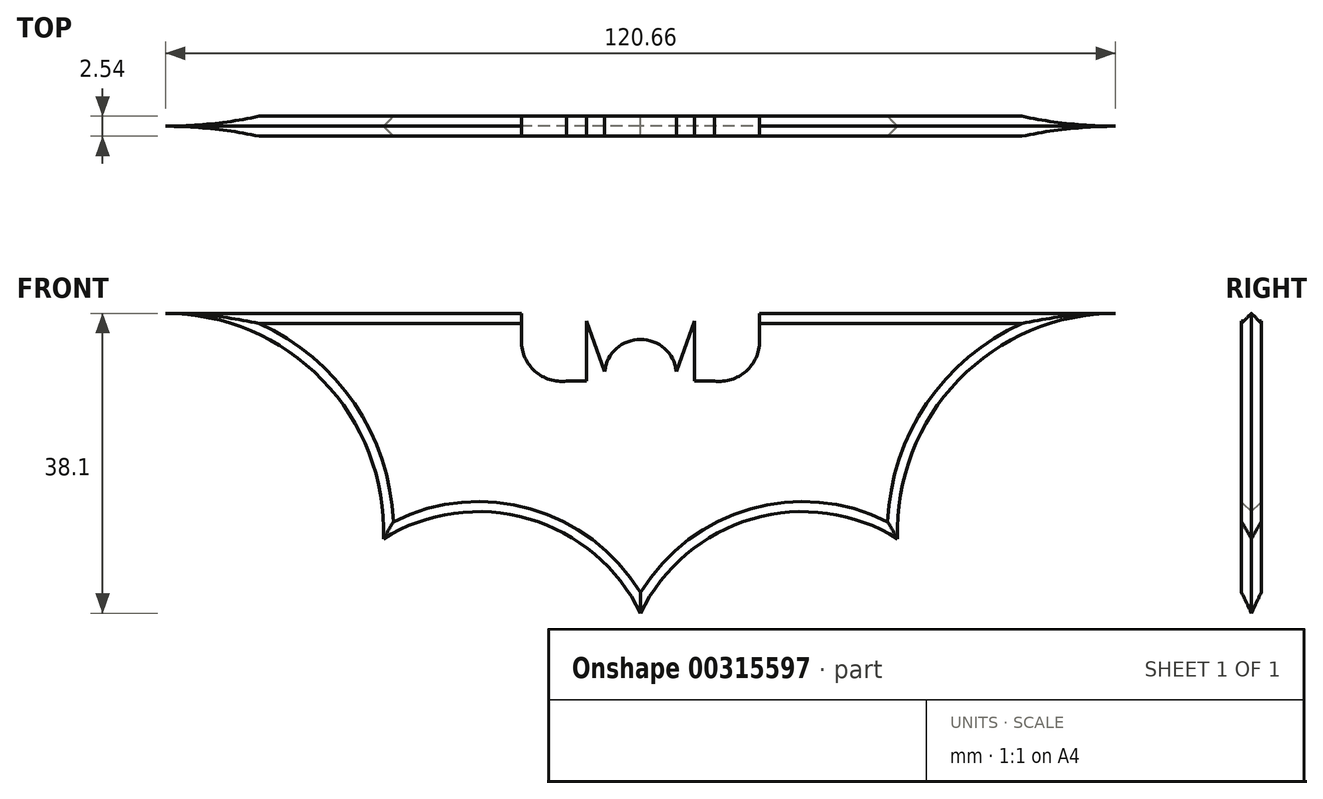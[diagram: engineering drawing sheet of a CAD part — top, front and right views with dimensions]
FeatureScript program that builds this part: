
annotation { "Feature Type Name" : "Feature", "Feature Type Description" : "" }
export const myFeature = defineFeature(function(context is Context, id is Id, definition is map)
    precondition{}
    {
        {
            var Q0;
            Q0=qCreatedBy(makeId("Front.planeOp"),FACE);
            var sketch = newSketch(context, id + "F0", { "sketchPlane" : qUnion([Q0])});
            skLineSegment(sketch, "E0", {"start": v(-60.33, 14.99) * mm, "end": v(-15.11, 14.99) * mm});
            skArc(sketch, "E1", {"start": v(-32.66, -13.64) * mm, "mid": v(-40.42, 6.54) * mm, "end": v(-60.33, 14.99) * mm});
            skLineSegment(sketch, "E2", {"start": v(-15.11, 14.99) * mm, "end": v(-15.11, 11.43) * mm});
            skPoint(sketch, "E3.visualSharp", {"position": v(-15.11, 0) * mm});
            skArc(sketch, "E3.filletArc", {"start": v(-15.11, 11.43) * mm, "mid": v(-13.4, 7.62) * mm, "end": v(-9.4, 6.39) * mm});
            skPoint(sketch, "E4", {"position": v(0, -23.11) * mm});
            skArc(sketch, "E5", {"start": v(4.54, 7.62) * mm, "mid": v(0, 11.68) * mm, "end": v(-4.54, 7.62) * mm});
            skLineSegment(sketch, "E6", {"start": v(-4.54, 7.62) * mm, "end": v(-6.87, 14) * mm});
            skLineSegment(sketch, "E7.MirrorCS", {"start": v(4.54, 7.62) * mm, "end": v(6.87, 14) * mm});
            skLineSegment(sketch, "E8.MirrorCS", {"start": v(6.87, 6.39) * mm, "end": v(6.87, 14) * mm});
            skArc(sketch, "E9", {"start": v(0, -23.11) * mm, "mid": v(-14.22, -11.1) * mm, "end": v(-32.66, -13.64) * mm});
            skArc(sketch, "E10.MirrorCS", {"start": v(-4.54, 7.62) * mm, "mid": v(0, 11.68) * mm, "end": v(4.54, 7.62) * mm});
            skLineSegment(sketch, "E11.MirrorCS", {"start": v(15.11, 14.99) * mm, "end": v(15.11, 11.43) * mm});
            skArc(sketch, "E12.MirrorCS", {"start": v(15.11, 11.43) * mm, "mid": v(13.4, 7.62) * mm, "end": v(9.4, 6.39) * mm});
            skArc(sketch, "E13.MirrorCS", {"start": v(0, -23.11) * mm, "mid": v(14.22, -11.1) * mm, "end": v(32.66, -13.64) * mm});
            skPoint(sketch, "E14.MirrorP", {"position": v(15.11, 0) * mm});
            skLineSegment(sketch, "E15.MirrorCS", {"start": v(60.33, 14.99) * mm, "end": v(15.11, 14.99) * mm});
            skArc(sketch, "E16.MirrorCS", {"start": v(32.66, -13.64) * mm, "mid": v(40.42, 6.54) * mm, "end": v(60.33, 14.99) * mm});
            skLineSegment(sketch, "E17", {"start": v(9.4, 6.39) * mm, "end": v(6.87, 6.39) * mm});
            skLineSegment(sketch, "E18", {"start": v(-6.87, 6.39) * mm, "end": v(-9.4, 6.39) * mm});
            skLineSegment(sketch, "E19", {"start": v(4.54, 7.62) * mm, "end": v(-4.54, 7.62) * mm, "construction": true});
            skLineSegment(sketch, "E20", {"start": v(-6.87, 14) * mm, "end": v(-6.87, 6.39) * mm});
            skLineSegment(sketch, "E21", {"start": v(0, -23.11) * mm, "end": v(0, 11.68) * mm, "construction": true});
            skLineSegment(sketch, "E22", {"start": v(-15.11, 0) * mm, "end": v(15.11, 0) * mm, "construction": true});
            skPoint(sketch, "E23", {"position": v(0, 0) * mm});
            skSolve(sketch);
        }
        {
            var Q0;
            Q0 = qSketchRegion(id + "F0", true);
            extrude(context, id + "F1", {"entities" : qUnion([Q0]), "endBound" : BoundingType.SYMMETRIC, "depth" : 2.54 * mm});
        }
        {
            var Q0;
            Q0=makeQuery(id+"F1.opExtrude","CAP_EDGE",EDGE,{"disambiguationData":[OSD([sQuery(id+"F0.wireOp",EDGE,"E1")])],"isStart":false});
            var Q1;
            Q1=makeQuery(id+"F1.opExtrude","CAP_EDGE",EDGE,{"disambiguationData":[OSD([sQuery(id+"F0.wireOp",EDGE,"E0")])],"isStart":false});
            var Q2;
            Q2=makeQuery(id+"F1.opExtrude","CAP_EDGE",EDGE,{"disambiguationData":[OSD([sQuery(id+"F0.wireOp",EDGE,"64feef33-b3c2-4a09-94ac-eb1fc36e8bcb.trimOffspring")])],"isStart":false});
            var Q3;
            Q3=makeQuery(id+"F1.opExtrude","CAP_EDGE",EDGE,{"disambiguationData":[OSD([sQuery(id+"F0.wireOp",EDGE,"5e13b118-4ba9-4713-bd14-634e33eb0e4a0.MirrorCS")])],"isStart":false});
            var Q4;
            Q4=makeQuery(id+"F1.opExtrude","CAP_EDGE",EDGE,{"disambiguationData":[OSD([sQuery(id+"F0.wireOp",EDGE,"6074a1c0-b8c4-469f-9281-2e97b01a270a0.MirrorCS")])],"isStart":false});
            var Q5;
            Q5=makeQuery(id+"F1.opExtrude","CAP_EDGE",EDGE,{"disambiguationData":[OSD([sQuery(id+"F0.wireOp",EDGE,"E9")])],"isStart":false});
            var Q6;
            Q6=makeQuery(id+"F1.opExtrude","CAP_EDGE",EDGE,{"disambiguationData":[OSD([sQuery(id+"F0.wireOp",EDGE,"5e13b118-4ba9-4713-bd14-634e33eb0e4a0.MirrorCS")])],"isStart":true});
            var Q7;
            Q7=makeQuery(id+"F1.opExtrude","CAP_EDGE",EDGE,{"disambiguationData":[OSD([sQuery(id+"F0.wireOp",EDGE,"64feef33-b3c2-4a09-94ac-eb1fc36e8bcb.trimOffspring")])],"isStart":true});
            var Q8;
            Q8=makeQuery(id+"F1.opExtrude","CAP_EDGE",EDGE,{"disambiguationData":[OSD([sQuery(id+"F0.wireOp",EDGE,"6074a1c0-b8c4-469f-9281-2e97b01a270a0.MirrorCS")])],"isStart":true});
            var Q9;
            Q9=makeQuery(id+"F1.opExtrude","CAP_EDGE",EDGE,{"disambiguationData":[OSD([sQuery(id+"F0.wireOp",EDGE,"E9")])],"isStart":true});
            var Q10;
            Q10=makeQuery(id+"F1.opExtrude","CAP_EDGE",EDGE,{"disambiguationData":[OSD([sQuery(id+"F0.wireOp",EDGE,"E1")])],"isStart":true});
            var Q11;
            Q11=makeQuery(id+"F1.opExtrude","CAP_EDGE",EDGE,{"disambiguationData":[OSD([sQuery(id+"F0.wireOp",EDGE,"E0")])],"isStart":true});
            var Q12;
            Q12=makeQuery(id+"F1.opExtrude","CAP_EDGE",EDGE,{"disambiguationData":[OSD([sQuery(id+"F0.wireOp",EDGE,"E15.MirrorCS")])],"isStart":false});
            var Q13;
            Q13=makeQuery(id+"F1.opExtrude","CAP_EDGE",EDGE,{"disambiguationData":[OSD([sQuery(id+"F0.wireOp",EDGE,"E16.MirrorCS")])],"isStart":false});
            var Q14;
            Q14=makeQuery(id+"F1.opExtrude","CAP_EDGE",EDGE,{"disambiguationData":[OSD([sQuery(id+"F0.wireOp",EDGE,"E13.MirrorCS")])],"isStart":false});
            var Q15;
            Q15=makeQuery(id+"F1.opExtrude","CAP_EDGE",EDGE,{"disambiguationData":[OSD([sQuery(id+"F0.wireOp",EDGE,"E15.MirrorCS")])],"isStart":true});
            var Q16;
            Q16=makeQuery(id+"F1.opExtrude","CAP_EDGE",EDGE,{"disambiguationData":[OSD([sQuery(id+"F0.wireOp",EDGE,"E16.MirrorCS")])],"isStart":true});
            var Q17;
            Q17=makeQuery(id+"F1.opExtrude","CAP_EDGE",EDGE,{"disambiguationData":[OSD([sQuery(id+"F0.wireOp",EDGE,"E13.MirrorCS")])],"isStart":true});
            chamfer(context, id + "F2", {"entities" : qUnion([Q0, Q1, Q2, Q3, Q4, Q5, Q6, Q7, Q8, Q9, Q10, Q11, Q12, Q13, Q14, Q15, Q16, Q17]), "width" : 1.27 * mm, "tangentPropagation" : true});
        }
    });
